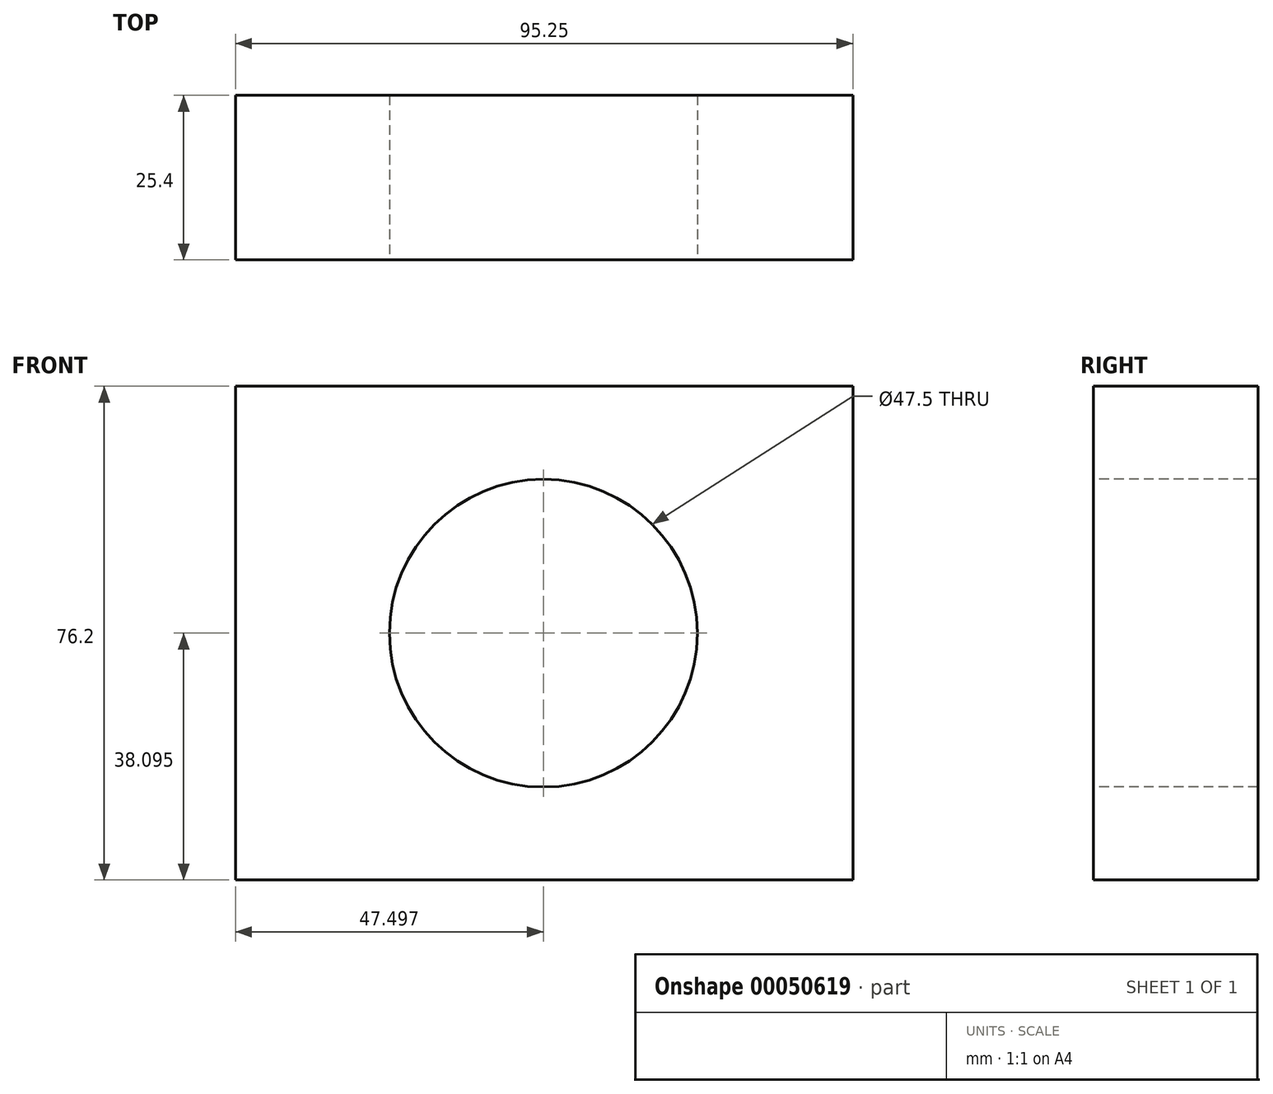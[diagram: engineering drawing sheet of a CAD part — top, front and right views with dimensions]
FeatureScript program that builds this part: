
annotation { "Feature Type Name" : "Feature", "Feature Type Description" : "" }
export const myFeature = defineFeature(function(context is Context, id is Id, definition is map)
    precondition{}
    {
        {
            var Q0;
            Q0=qCreatedBy(makeId("Front.planeOp"),FACE);
            var sketch = newSketch(context, id + "F0", { "sketchPlane" : qUnion([Q0])});
            skLineSegment(sketch, "E0.bottom", {"start": v(-62.7, 68.17) * mm, "end": v(32.56, 68.17) * mm});
            skLineSegment(sketch, "E0.top", {"start": v(-62.7, -8.03) * mm, "end": v(32.56, -8.03) * mm});
            skLineSegment(sketch, "E0.left", {"start": v(-62.7, 68.17) * mm, "end": v(-62.7, -8.03) * mm});
            skLineSegment(sketch, "E0.right", {"start": v(32.56, 68.17) * mm, "end": v(32.56, -8.03) * mm});
            skSolve(sketch);
        }
        {
            var Q0;
            Q0 = qSketchRegion(id + "F0", true);
            extrude(context, id + "F1", {"entities" : qUnion([Q0]), "depth" : 25.4 * mm});
        }
        {
            var Q0;
            Q0=makeQuery(id+"F1.opExtrude","CAP_FACE",FACE,{"disambiguationData":[OSD([sQuery(id+"F0.wireOp",EDGE,"E0.bottom"),sQuery(id+"F0.wireOp",EDGE,"E0.top"),sQuery(id+"F0.wireOp",EDGE,"E0.left"),sQuery(id+"F0.wireOp",EDGE,"E0.right")])],"isStart":false});
            var sketch = newSketch(context, id + "F2", { "sketchPlane" : qUnion([Q0])});
            skLineSegment(sketch, "E1.0", {"start": v(-15.2, 68.17) * mm, "end": v(-15.2, -8.03) * mm, "construction": true});
            skLineSegment(sketch, "E2.0", {"start": v(26.2, 61.82) * mm, "end": v(-56.34, 61.82) * mm, "construction": true});
            skLineSegment(sketch, "E2.1", {"start": v(26.2, -1.68) * mm, "end": v(26.2, 61.82) * mm, "construction": true});
            skLineSegment(sketch, "E2.2", {"start": v(-56.34, -1.68) * mm, "end": v(26.2, -1.68) * mm, "construction": true});
            skLineSegment(sketch, "E2.3", {"start": v(-56.34, 61.82) * mm, "end": v(-56.34, -1.68) * mm, "construction": true});
            skCircle(sketch, "E3", {"center": v(-15.2, 30.07) * mm, "radius": 23.75 * mm});
            skSolve(sketch);
        }
        {
            var Q0;
            Q0 = qSketchRegion(id + "F2", true);
            extrude(context, id + "F3", {"entities" : qUnion([Q0]), "operationType" : NewBodyOperationType.REMOVE, "endBound" : BoundingType.THROUGH_ALL, "oppositeDirection" : true, "depth" : 25.4 * mm});
        }
    });
